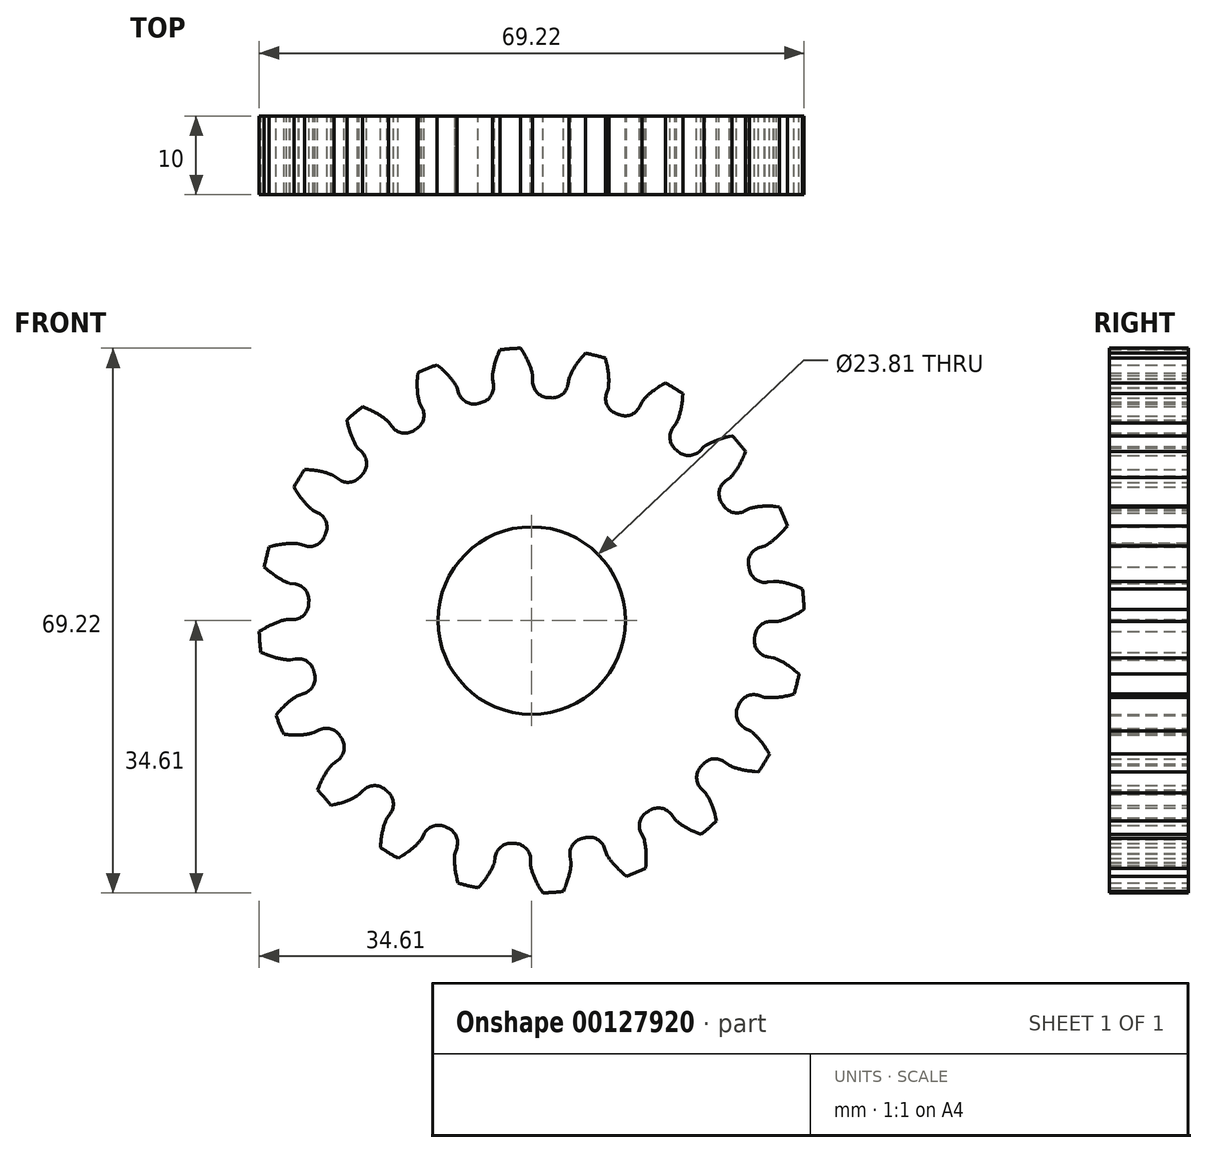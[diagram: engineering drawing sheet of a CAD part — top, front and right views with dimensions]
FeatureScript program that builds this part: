
annotation { "Feature Type Name" : "Feature", "Feature Type Description" : "" }
export const myFeature = defineFeature(function(context is Context, id is Id, definition is map)
    precondition{}
    {
        {
            assignVariable(context, id + "F0", {"name" : "Teeth", "anyValue" : 20});
        }
        {
            var Q0;
            Q0=qCreatedBy(makeId("Front.planeOp"),FACE);
            var sketch = newSketch(context, id + "F1", { "sketchPlane" : qUnion([Q0])});
            skCircle(sketch, "E0", {"center": v(0, 0) * mm, "radius": 3.07 * mm, "construction": true});
            skLineSegment(sketch, "E1", {"start": v(0, 0) * mm, "end": v(-0.14, 3.07) * mm, "construction": true});
            skLineSegment(sketch, "E2", {"start": v(0, 0) * mm, "end": v(-0.3, 3.06) * mm, "construction": true});
            skLineSegment(sketch, "E3", {"start": v(0, 0) * mm, "end": v(-0.47, 3.04) * mm, "construction": true});
            skLineSegment(sketch, "E4", {"start": v(-0.47, 3.04) * mm, "end": v(0.01, 3.11) * mm, "construction": true});
            skLineSegment(sketch, "E5", {"start": v(0, 0) * mm, "end": v(-0.62, 3) * mm, "construction": true});
            skLineSegment(sketch, "E6", {"start": v(-0.62, 3) * mm, "end": v(0, 3.14) * mm, "construction": true});
            skLineSegment(sketch, "E7", {"start": v(-0.47, 3.04) * mm, "end": v(-0.3, 3.06) * mm, "construction": true});
            skLineSegment(sketch, "E8", {"start": v(-0.62, 3) * mm, "end": v(-0.47, 3.04) * mm, "construction": true});
            skLineSegment(sketch, "E9", {"start": v(-0.47, 3.04) * mm, "end": v(-0.14, 3.07) * mm, "construction": true});
            skLineSegment(sketch, "E10", {"start": v(-0.62, 3) * mm, "end": v(-0.14, 3.07) * mm, "construction": true});
            skLineSegment(sketch, "E11", {"start": v(0, 0) * mm, "end": v(-1.09, 2.87) * mm, "construction": true});
            skLineSegment(sketch, "E12", {"start": v(-1.09, 2.87) * mm, "end": v(-0.04, 3.27) * mm, "construction": true});
            skLineSegment(sketch, "E13", {"start": v(0, 0) * mm, "end": v(-0.94, 2.93) * mm, "construction": true});
            skLineSegment(sketch, "E14", {"start": v(-0.94, 2.93) * mm, "end": v(-0.02, 3.22) * mm, "construction": true});
            skLineSegment(sketch, "E15", {"start": v(0, 0) * mm, "end": v(-0.78, 2.97) * mm, "construction": true});
            skLineSegment(sketch, "E16", {"start": v(-0.78, 2.97) * mm, "end": v(0, 3.18) * mm, "construction": true});
            skLineSegment(sketch, "E17", {"start": v(-0.78, 2.97) * mm, "end": v(-0.62, 3) * mm, "construction": true});
            skLineSegment(sketch, "E18", {"start": v(-0.78, 2.97) * mm, "end": v(-0.94, 2.93) * mm, "construction": true});
            skLineSegment(sketch, "E19", {"start": v(-0.94, 2.93) * mm, "end": v(-1.09, 2.87) * mm, "construction": true});
            skLineSegment(sketch, "E20", {"start": v(-0.78, 2.97) * mm, "end": v(-0.14, 3.07) * mm, "construction": true});
            skLineSegment(sketch, "E21", {"start": v(-0.94, 2.93) * mm, "end": v(-0.14, 3.07) * mm, "construction": true});
            skLineSegment(sketch, "E22", {"start": v(-1.09, 2.87) * mm, "end": v(-0.14, 3.07) * mm, "construction": true});
            skLineSegment(sketch, "E23", {"start": v(0, 0) * mm, "end": v(-1.38, 2.74) * mm, "construction": true});
            skLineSegment(sketch, "E24", {"start": v(-1.38, 2.74) * mm, "end": v(-0.1, 3.4) * mm, "construction": true});
            skLineSegment(sketch, "E25", {"start": v(0, 0) * mm, "end": v(-1.53, 2.67) * mm, "construction": true});
            skLineSegment(sketch, "E26", {"start": v(-1.53, 2.67) * mm, "end": v(-0.14, 3.46) * mm, "construction": true});
            skLineSegment(sketch, "E27", {"start": v(0, 0) * mm, "end": v(-1.66, 2.58) * mm, "construction": true});
            skLineSegment(sketch, "E28", {"start": v(0, 0) * mm, "end": v(-1.24, 2.81) * mm, "construction": true});
            skLineSegment(sketch, "E29", {"start": v(-1.24, 2.81) * mm, "end": v(-0.06, 3.33) * mm, "construction": true});
            skLineSegment(sketch, "E30", {"start": v(-1.09, 2.87) * mm, "end": v(-1.24, 2.81) * mm, "construction": true});
            skLineSegment(sketch, "E31", {"start": v(-1.24, 2.81) * mm, "end": v(-1.38, 2.74) * mm, "construction": true});
            skLineSegment(sketch, "E32", {"start": v(-1.38, 2.74) * mm, "end": v(-1.53, 2.67) * mm, "construction": true});
            skLineSegment(sketch, "E33", {"start": v(-1.53, 2.67) * mm, "end": v(-1.66, 2.58) * mm, "construction": true});
            skLineSegment(sketch, "E34", {"start": v(-0.14, 3.07) * mm, "end": v(-1.24, 2.81) * mm, "construction": true});
            skLineSegment(sketch, "E35", {"start": v(-0.14, 3.07) * mm, "end": v(-1.38, 2.74) * mm, "construction": true});
            skLineSegment(sketch, "E36", {"start": v(-0.14, 3.07) * mm, "end": v(-1.53, 2.67) * mm, "construction": true});
            skLineSegment(sketch, "E37", {"start": v(-0.14, 3.07) * mm, "end": v(-1.66, 2.58) * mm, "construction": true});
            skCircle(sketch, "E38", {"center": v(0, 0) * mm, "radius": 3.18 * mm, "construction": true});
            skCircle(sketch, "E39", {"center": v(0, 0) * mm, "radius": 3.46 * mm});
            skPoint(sketch, "E40", {"position": v(0, 3.18) * mm});
            skLineSegment(sketch, "E41", {"start": v(0, 0) * mm, "end": v(-0.67, 8.57) * mm, "construction": true});
            skPoint(sketch, "E42.MirrorP", {"position": v(-0.5, 3.14) * mm});
            skLineSegment(sketch, "E43", {"start": v(-0.5, 3.14) * mm, "end": v(0, 0) * mm, "construction": true});
            skLineSegment(sketch, "E44", {"start": v(0, 0) * mm, "end": v(0, 3.18) * mm, "construction": true});
            skLineSegment(sketch, "E45", {"start": v(-0.3, 3.06) * mm, "end": v(-0.14, 3.07) * mm, "construction": true});
            skLineSegment(sketch, "E46", {"start": v(0.01, 3.11) * mm, "end": v(0, 3.14) * mm, "construction": true});
            skLineSegment(sketch, "E47", {"start": v(0, 0) * mm, "end": v(0, 10.19) * mm, "construction": true});
            skCircle(sketch, "E48", {"center": v(0, 0) * mm, "radius": 2.84 * mm});
            skSolve(sketch);
        }
        {
            var Q0;
            Q0=qCreatedBy(makeId("Front.planeOp"),FACE);
            var sketch = newSketch(context, id + "F2", { "sketchPlane" : qUnion([Q0])});
            skCircle(sketch, "E49.0", {"center": v(0, 0) * mm, "radius": 3.18 * mm, "construction": true});
            skPoint(sketch, "E50.0", {"position": v(-0.14, 3.46) * mm});
            skPoint(sketch, "E50.1", {"position": v(-0.1, 3.4) * mm});
            skPoint(sketch, "E50.2", {"position": v(-0.06, 3.33) * mm});
            skPoint(sketch, "E50.3", {"position": v(-0.04, 3.27) * mm});
            skPoint(sketch, "E50.4", {"position": v(-0.02, 3.22) * mm});
            skPoint(sketch, "E50.6", {"position": v(0, 3.14) * mm});
            skPoint(sketch, "E50.7", {"position": v(0.01, 3.11) * mm});
            skPoint(sketch, "E50.8", {"position": v(0, 3.18) * mm});
            skLineSegment(sketch, "E51.0", {"start": v(0, 0) * mm, "end": v(-0.67, 8.57) * mm, "construction": true});
            skFitSpline(sketch, "E52", {"points": [v(-0.14, 3.46) * mm, v(-0.1, 3.4) * mm, v(-0.06, 3.33) * mm, v(-0.04, 3.27) * mm, v(-0.02, 3.22) * mm, v(0, 3.18) * mm, v(0, 3.14) * mm, v(0.01, 3.11) * mm], "startDerivative": vector(0.73, -1.17) * mm, "endDerivative": vector(0.17, -0.82) * mm});
            skFitSpline(sketch, "E53.MirrorCS", {"points": [v(-0.4, 3.44) * mm, v(-0.43, 3.37) * mm, v(-0.46, 3.3) * mm, v(-0.47, 3.24) * mm, v(-0.49, 3.18) * mm, v(-0.5, 3.14) * mm, v(-0.5, 3.1) * mm, v(-0.5, 3.07) * mm], "startDerivative": vector(-0.53, -1.26) * mm, "endDerivative": vector(-0.04, -0.84) * mm});
            skCircle(sketch, "E54", {"center": v(0, 0) * mm, "radius": 1.2 * mm});
            skCircle(sketch, "E55.0", {"center": v(0, 0) * mm, "radius": 2.84 * mm});
            skArc(sketch, "E56", {"start": v(-0.14, 3.46) * mm, "mid": v(-0.27, 3.45) * mm, "end": v(-0.4, 3.44) * mm});
            skLineSegment(sketch, "E57", {"start": v(-0.5, 3.07) * mm, "end": v(0, 0) * mm});
            skLineSegment(sketch, "E58", {"start": v(0, 0) * mm, "end": v(0.01, 3.11) * mm});
            skSolve(sketch);
        }
        {
            var Q0;
            {var subQ1=sQuery(id+"F2.wireOp",EDGE,"E52");var subQ9=sQuery(id+"F2.wireOp",EDGE,"rA0usyOi-Jm6w-jZNR-JSDv-ujEcH4bsm2Ol");var subQ11=makeQuery(id+"F2.imprint","INTERSECT",VERTEX,{"derivedFrom":[subQ1,subQ9]});Q0=makeQuery(id+"F2.imprint","IMPRINT",FACE,{"disambiguationData":[TD([[makeQuery(id+"F2.imprint","IMPRINT",EDGE,{"disambiguationData":[TD([[subQ11,1.0]])],"derivedFrom":subQ1}),-1.0]])]});}
            var Q1;
            {var subQ0=sQuery(id+"F2.wireOp",EDGE,"QqPcIgQ4-TZE6-73E5-WQaq-ugCT5JtziKyn");var subQ1=sQuery(id+"F2.wireOp",EDGE,"90be38e0-c88f-493d-85a8-1201295b9109.0");var subQ2=makeQuery(id+"F2.imprint","INTERSECT",VERTEX,{"derivedFrom":[subQ1,subQ0]});Q1=makeQuery(id+"F2.imprint","IMPRINT",FACE,{"disambiguationData":[TD([[makeQuery(id+"F2.imprint","IMPRINT",EDGE,{"disambiguationData":[TD([[subQ2,1.0]])],"derivedFrom":subQ1}),1.0]])]});}
            var Q2;
            {var subQ0=sQuery(id+"F2.wireOp",EDGE,"QqPcIgQ4-TZE6-73E5-WQaq-ugCT5JtziKyn");var subQ1=sQuery(id+"F2.wireOp",EDGE,"90be38e0-c88f-493d-85a8-1201295b9109.0");var subQ2=makeQuery(id+"F2.imprint","INTERSECT",VERTEX,{"derivedFrom":[subQ1,subQ0]});Q2=makeQuery(id+"F2.imprint","IMPRINT",FACE,{"disambiguationData":[TD([[makeQuery(id+"F2.imprint","IMPRINT",EDGE,{"disambiguationData":[TD([[subQ2,-1.0]])],"derivedFrom":subQ1}),1.0]])]});}
            var Q3;
            {var subQ1=sQuery(id+"F2.wireOp",EDGE,"E52");var subQ8=sQuery(id+"F2.wireOp",EDGE,"b861a5ab-cd51-40f1-92ab-cea0f5fe0d4d.1");var subQ11=makeQuery(id+"F2.imprint","INTERSECT",VERTEX,{"derivedFrom":[subQ1,subQ8]});Q3=makeQuery(id+"F2.imprint","IMPRINT",FACE,{"disambiguationData":[TD([[makeQuery(id+"F2.imprint","IMPRINT",EDGE,{"disambiguationData":[TD([[subQ11,1.0]])],"derivedFrom":subQ1}),-1.0]])]});}
            var Q4;
            {var subQ0=sQuery(id+"F2.wireOp",EDGE,"b861a5ab-cd51-40f1-92ab-cea0f5fe0d4d.0");var subQ1=sQuery(id+"F2.wireOp",EDGE,"E54");var subQ2=makeQuery(id+"F2.imprint","INTERSECT",VERTEX,{"derivedFrom":[subQ1,subQ0]});Q4=makeQuery(id+"F2.imprint","IMPRINT",FACE,{"disambiguationData":[TD([[makeQuery(id+"F2.imprint","IMPRINT",EDGE,{"disambiguationData":[TD([[subQ2,-1.0]])],"derivedFrom":subQ1}),-1.0]])]});}
            var Q5;
            {var subQ0=sQuery(id+"F2.wireOp",EDGE,"b861a5ab-cd51-40f1-92ab-cea0f5fe0d4d.0");var subQ1=sQuery(id+"F2.wireOp",EDGE,"E54");var subQ2=makeQuery(id+"F2.imprint","INTERSECT",VERTEX,{"derivedFrom":[subQ1,subQ0]});Q5=makeQuery(id+"F2.imprint","IMPRINT",FACE,{"disambiguationData":[TD([[makeQuery(id+"F2.imprint","IMPRINT",EDGE,{"disambiguationData":[TD([[subQ2,1.0]])],"derivedFrom":subQ1}),-1.0]])]});}
            extrude(context, id + "F3", {"entities" : qUnion([Q0, Q1, Q2, Q3, Q4, Q5]), "depth" : 1 * mm});
        }
        {
            var Q0;
            Q0=makeQuery(id+"F3.opExtrude","SWEPT_EDGE",EDGE,{"disambiguationData":[OSD([sQuery(id+"F2.wireOp",EDGE,"b861a5ab-cd51-40f1-92ab-cea0f5fe0d4d.1"),sQuery(id+"F2.wireOp",EDGE,"E55.0")])]});
            var Q1;
            Q1=makeQuery(id+"F3.opExtrude","SWEPT_EDGE",EDGE,{"disambiguationData":[OSD([sQuery(id+"F2.wireOp",EDGE,"b861a5ab-cd51-40f1-92ab-cea0f5fe0d4d.0"),sQuery(id+"F2.wireOp",EDGE,"E55.0")])]});
            fillet(context, id + "F4", {"entities" : qUnion([Q0, Q1]), "radius" : 0.2 * mm, "tangentPropagation" : true, "allowEdgeOverflow" : false});
        }
        {
            var Q0;
            Q0=makeQuery(id+"F4.opFillet","BLEND_FACE",FACE,{"disambiguationData":[OSD([sQuery(id+"F2.wireOp",EDGE,"E55.0"),sQuery(id+"F2.wireOp",EDGE,"E57")])]});
            var Q1;
            Q1=makeQuery(id+"F3.opExtrude","SWEPT_FACE",FACE,{"disambiguationData":[OSD([sQuery(id+"F2.wireOp",EDGE,"E57")])]});
            var Q2;
            Q2=makeQuery(id+"F3.opExtrude","SWEPT_FACE",FACE,{"disambiguationData":[OSD([sQuery(id+"F2.wireOp",EDGE,"E53.MirrorCS")])]});
            var Q3;
            Q3=makeQuery(id+"F3.opExtrude","SWEPT_FACE",FACE,{"disambiguationData":[OSD([sQuery(id+"F2.wireOp",EDGE,"E56")])]});
            var Q4;
            Q4=makeQuery(id+"F3.opExtrude","SWEPT_FACE",FACE,{"disambiguationData":[OSD([sQuery(id+"F2.wireOp",EDGE,"E52")])]});
            var Q5;
            Q5=makeQuery(id+"F3.opExtrude","SWEPT_FACE",FACE,{"disambiguationData":[OSD([sQuery(id+"F2.wireOp",EDGE,"E58")])]});
            var Q6;
            Q6=makeQuery(id+"F4.opFillet","BLEND_FACE",FACE,{"disambiguationData":[OSD([sQuery(id+"F2.wireOp",EDGE,"E55.0"),sQuery(id+"F2.wireOp",EDGE,"E58")])]});
            var Q7;
            Q7=makeQuery(id+"F3.opExtrude","SWEPT_FACE",FACE,{"disambiguationData":[OSD([sQuery(id+"F2.wireOp",EDGE,"E55.0")])]});
            circularPattern(context, id + "F5", {"faces" : qUnion([Q0, Q1, Q2, Q3, Q4, Q5, Q6]), "axis" : qUnion([Q7]), "angle" : 360 * degree, "instanceCount" : round(getVariable(context, 'Teeth')), "equalSpace" : true, "patternType" : PatternType.FACE, "computeTransformsWithoutBuiltin" : true});
        }
        {
            var Q0;
            Q0=makeQuery(id+"F3.opExtrude","SWEPT_BODY",BODY,{"disambiguationData":[OSD([sQuery(id+"F2.wireOp",EDGE,"E52"),sQuery(id+"F2.wireOp",EDGE,"E53.MirrorCS"),sQuery(id+"F2.wireOp",EDGE,"E54"),sQuery(id+"F2.wireOp",EDGE,"E55.0"),sQuery(id+"F2.wireOp",EDGE,"E56"),sQuery(id+"F2.wireOp",EDGE,"E57"),sQuery(id+"F2.wireOp",EDGE,"E58")])]});
            var Q1;
            Q1=qCreatedBy(makeId("Origin.pointOp"),VERTEX);
            transform(context, id + "F6", {"entities" : qUnion([Q0]), "transformType" : TransformType.SCALE_UNIFORMLY, "scale" : 10, "scalePoint" : qUnion([Q1]), "makeCopy" : false});
        }
    });
